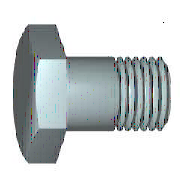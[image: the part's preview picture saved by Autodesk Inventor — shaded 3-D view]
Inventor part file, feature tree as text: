
AUTODESK INVENTOR PART (.ipt)
format: ipt  version: 2021 (Build 250183000, 183)  size: 192,512 bytes
history: native  units: mm (DEFAULTED — no unit token found)
features: sketch x3, extrude x1, chamfer x1, plane x1
ambient origin geometry x7: Origin, YZ Plane, XZ Plane, X Axis, Y Axis, Z Axis, Center Point
bodies: Solid1 (feature_tree), Body (feature_tree)
feature tree (6):
  extrude  "Head"  Depth=22.0mm
  chamfer  "Chamfer1"  Distance=4.7mm
  plane  "Work Plane1"
  sketch  "Sketch1"  dims[d0=40.0mm d1=22.0mm]
  sketch  "Sketch2"  dims[d2=8.0mm]
  sketch  "Sketch4"  dims[d12=90.0deg d3=4.7mm d4=0.0mm d5=30.0deg d21=90.0deg d6=0.766813mm d7=0.766912mm d8=0.0mm d9=0.6001mm d10=11.63mm d11=13.0mm d13=0.766912mm d14=8.0mm d15=22.0mm d16=0.0mm d19=13.0mm d55=45.0deg d57=0.0mm d58=0.0mm]
